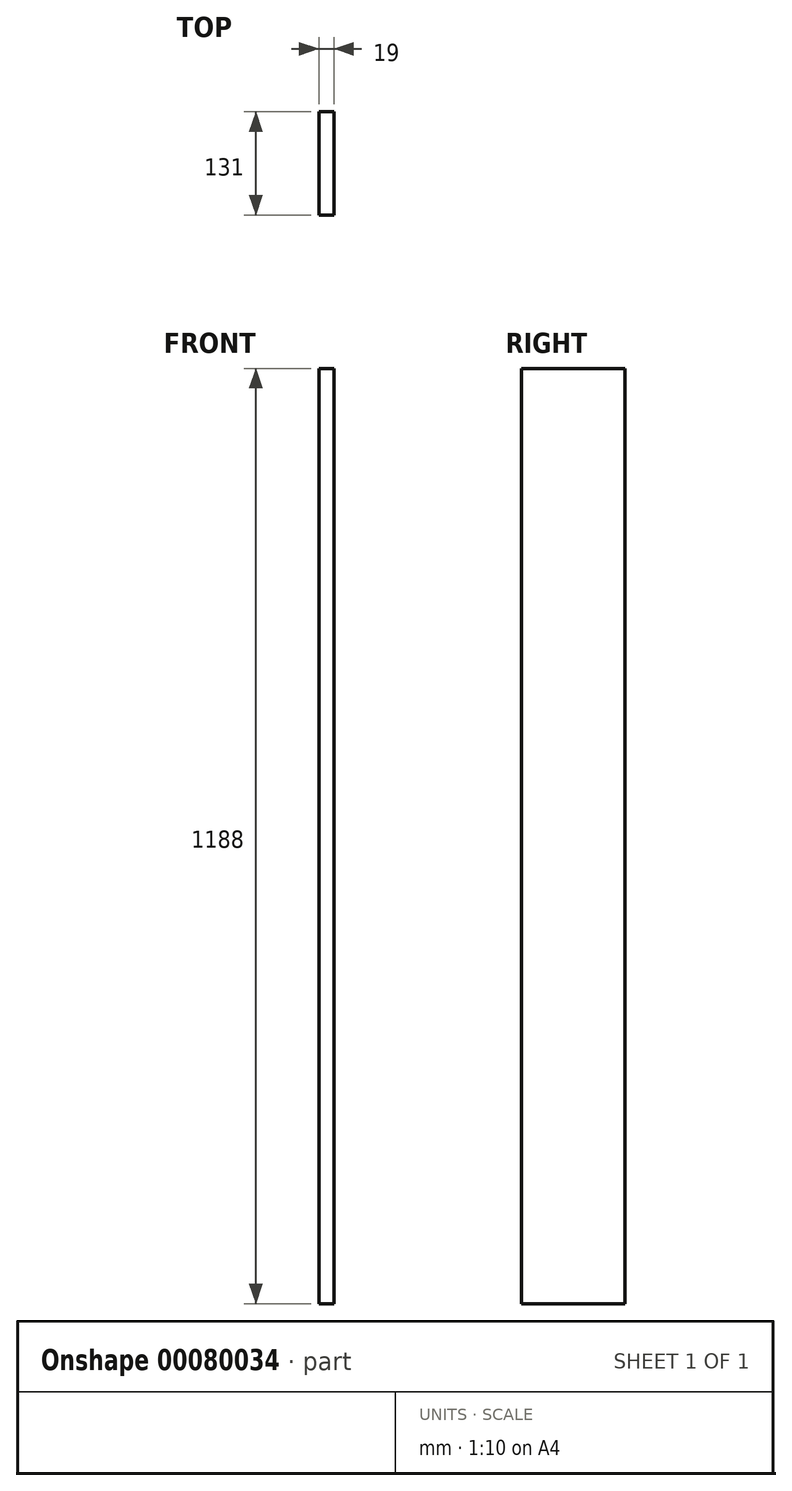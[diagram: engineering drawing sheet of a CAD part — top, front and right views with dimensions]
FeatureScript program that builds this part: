
annotation { "Feature Type Name" : "Feature", "Feature Type Description" : "" }
export const myFeature = defineFeature(function(context is Context, id is Id, definition is map)
    precondition{}
    {
        {
            var Q0;
            Q0=qCreatedBy(makeId("Right.planeOp"),FACE);
            var sketch = newSketch(context, id + "F0", { "sketchPlane" : qUnion([Q0])});
            skLineSegment(sketch, "E0.bottom", {"start": v(0, 0) * mm, "end": v(131, 0) * mm});
            skLineSegment(sketch, "E0.top", {"start": v(0, -1188) * mm, "end": v(131, -1188) * mm});
            skLineSegment(sketch, "E0.left", {"start": v(0, 0) * mm, "end": v(0, -1188) * mm});
            skLineSegment(sketch, "E0.right", {"start": v(131, 0) * mm, "end": v(131, -1188) * mm});
            skSolve(sketch);
        }
        {
            var Q0;
            Q0=makeQuery(id+"F0.imprint","IMPRINT",FACE,{"disambiguationData":[TD([[makeQuery(id+"F0.imprint","IMPRINT",EDGE,{"derivedFrom":sQuery(id+"F0.wireOp",EDGE,"E0.bottom")}),-1.0]])]});
            extrude(context, id + "F1", {"entities" : qUnion([Q0]), "depth" : 19 * mm});
        }
    });
